# Revit family: Plumbing-Flushometer-Sloan-Valve-TRF-8156_
name_source: partatom
category: Plumbing Fixtures
units: mm (PartAtom-declared; Revit-internal decimal feet)

## family parameters
Cut with Voids When Loaded = Yes
Host = Face
OmniClass Number = 23.45.05.14.99
OmniClass Title = Other Sanitary Washing Plumbing Fixtures
Part Type = Normal
Room Calculation Point = No
Round Connector Dimension = Use Diameter
Shared = No

## types (6) — shared parameters
Apparent Load = 0 VA
Assembly Code = D2020300
CW Connection = Yes
Current = 0 A
Default Elevation = 0"
Edition number = 1
HW Connection = No
Height = 6 1/4"
Keynote = 15410
Manufacturer = Sloan Valve
Number of Poles = 1
Operating Water Pressure = 15 – 80 PSI (103 – 552 kPa)
Power Factor = 1
Product data url = https://bimobject.com
URL = www.sloanvalve.com
Valve Pressure Drop = 0.00 psi
Vent Connection = No
Waste Connection = No
Water Inlet Connection Diameter = 2"
Water Outlet Connection Diameter = 2"
z_Array Length = 0"
zero-valued in all types: CWFU, HWFU, WFU

## per-type parameters (varying)
| type | Description | Flush Rate | Part Number | Product Material | Voltage | z_Array Count | z_Hardwired |
| TRF 8156-1.1-OR | 1.1 gpf, Filtered, Polished Chrome Finish, Fixture Connection Rear Spud, Single Flush, Integrated Control Stop, Electrical Override, Battery with Hardwired Option, Sensor-Operated, TruFlush Concealed Sensor Water Closet Flushometer. | 1.1 gpf (4.2 Lpf) | 34001005 | Sloan Valve - Finish - Polished Chrome | 6 V | 3 | Yes |
| TRF 8156-1.1-SF-OR | 1.1 gpf, Filtered, Brushed Stainless Finish, Fixture Connection Rear Spud, Single Flush, Integrated Control Stop, Electrical Override, Battery with Hardwired Option, Sensor-Operated, TruFlush Concealed Sensor Water Closet Flushometer. | 1.1 gpf (4.2 Lpf) | 34001006 | Sloan Valve - Finish - Brushed Stainless Steel | 6 V | 3 | Yes |
| TRF 8156-1.28-SF-OR | 1.28 gpf, Filtered, Brushed Stainless Finish, Fixture Connection Rear Spud, Single Flush, Electrical Override, Battery, TruFlush Concealed Sensor Water Closet Flushometer. | 1.28 gpf (4.8 Lpf) | 3400116 | Sloan Valve - Finish - Brushed Stainless Steel | 0 V | 2 | No |
| TRF 8156-1.6-SF-OR | 1.6 gpf, Filtered, Brushed Stainless Finish, Fixture Connection Rear Spud, Single Flush, Electrical Override, Battery, TruFlush Concealed Sensor Water Closet Flushometer. | 1.6 gpf (6.0 Lpf) | 3400115 | Sloan Valve - Finish - Brushed Stainless Steel | 0 V | 2 | No |
| TRF 8156-1.28-OR | 1.28 gpf, Filtered, Polished Chrome Finish, Fixture Connection Rear Spud, Single Flush, Electrical Override, Battery, TruFlush Concealed Sensor Water Closet Flushometer. | 1.28 gpf (4.8 Lpf) | 3400101 | Sloan Valve - Finish - Polished Chrome | 0 V | 2 | No |
| TRF 8156-1.6-OR | 1.6 gpf, Filtered, Polished Chrome Finish, Fixture Connection Rear Spud, Single Flush, Electrical Override, Battery, TruFlush Concealed Sensor Water Closet Flushometer. | 1.6 gpf (6.0 Lpf) | 3400100 | Sloan Valve - Finish - Polished Chrome | 0 V | 2 | No |

note: column(s) folded — value = type name in every type: Model

## geometry (parser evidence)
native form markers: Sweep x5
no freeform markers — native parametric forms only
